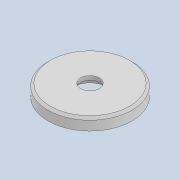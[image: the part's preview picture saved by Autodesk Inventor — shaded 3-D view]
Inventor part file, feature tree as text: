
AUTODESK INVENTOR PART (.ipt)
format: ipt  version: 2022 (Build 260153000, 153)  size: 115,200 bytes
history: native  units: mm
features: sketch x2, other x1, extrude x1, chamfer x1, hole x1
ambient origin geometry x8: Origin, YZ Plane, XZ Plane, XY Plane, X Axis, Y Axis, Z Axis, Center Point
bodies: Body1 (feature_tree)
feature tree (6):
  other  "Sólido1"
  extrude  "Extrusión1"  Depth=2.5mm TaperAngle=0.0deg
  chamfer  "Chaflán1"  Distance=2.0mm Angle=45.0deg
  hole  "Agujero1"  [1 undecoded]
  sketch  "Boceto1"  dims[d0=18.0mm d1=2.5mm d2=0.0mm d3=0.5mm d4=2.0mm d5=45.0deg]
  sketch  "Boceto2"  dims[d6=4.0mm d7=10.973mm d8=7.3mm d9=0.5mm d10=90.0deg d11=16.265mm d12=20.594885mm d13=1.0mm d14=1.0mm d15=1.0mm d16=0.15mm d17=0.25mm d18=0.375mm d19=14.3117mm d20=0.75mm d21=20.594885mm d22=0.0625mm d23=0.75mm d24=0.375mm]
note: 1 required parameter value undecoded (feature->parameter linkage not recoverable at this tier; creation-order binding heuristic only, values carry confidence <= 0.55)
